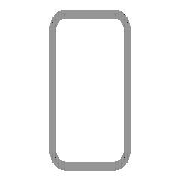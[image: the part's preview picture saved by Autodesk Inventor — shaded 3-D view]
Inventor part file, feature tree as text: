
AUTODESK INVENTOR PART (.ipt)
format: ipt  version: 2025 (Build 290162010, 162A)  size: 133,120 bytes
history: native  units: mm (DEFAULTED — no unit token found)
features: other x4, sketch x1, plane x1
ambient origin geometry x8: Origin, YZ Plane, XZ Plane, XY Plane, X Axis, Y Axis, Z Axis, Center Point
bodies: Solid1 (feature_tree), Body (feature_tree)
feature tree (6):
  parser-record x1  (decoder bookkeeping rows leaked as tree rows — omitted from the tree; the rows remain in map.json)
  other  "Driven Length"
  other  "Start Plane"
  other  "End Plane"
  sketch  "Sketch3"  dims[d3=250.0mm d4=0.0mm d7=4.0mm d9=20.0mm d11=40.0mm d12=2.0mm d13=-0.0mm d14=250.0mm d15=10.0mm d16=20.0mm d17=90.0deg d18=250.0mm]
  plane  "Work Plane3"
